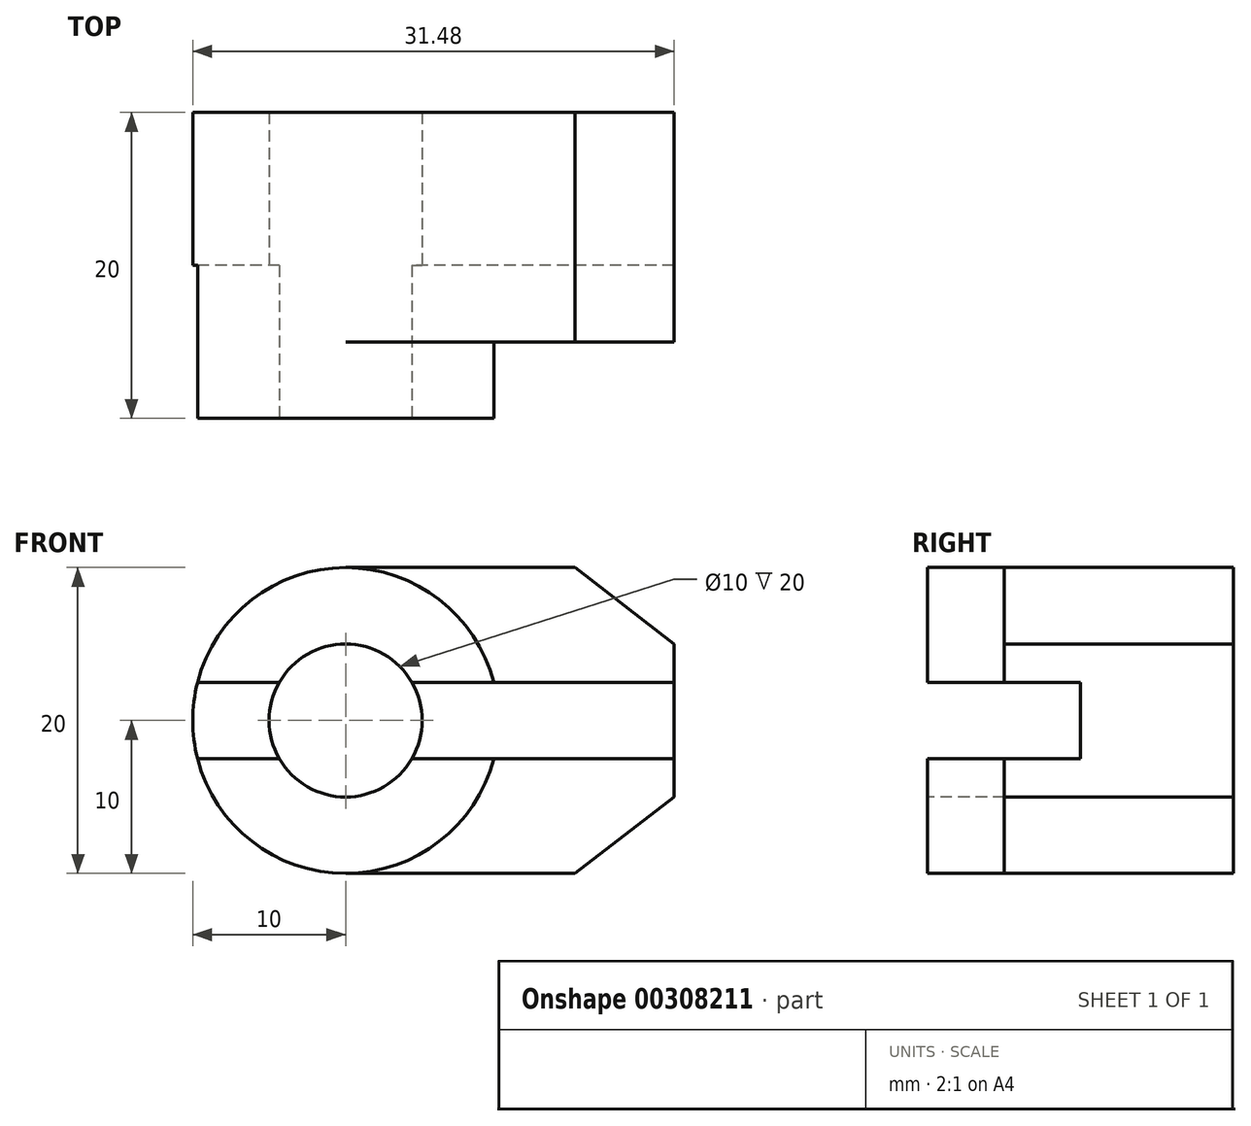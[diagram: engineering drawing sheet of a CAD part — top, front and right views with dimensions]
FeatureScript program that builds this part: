
annotation { "Feature Type Name" : "Feature", "Feature Type Description" : "" }
export const myFeature = defineFeature(function(context is Context, id is Id, definition is map)
    precondition{}
    {
        {
            var Q0;
            Q0=qCreatedBy(makeId("Front.planeOp"),FACE);
            var sketch = newSketch(context, id + "F0", { "sketchPlane" : qUnion([Q0])});
            skCircle(sketch, "E0", {"center": v(0, 10) * mm, "radius": 10 * mm});
            skSolve(sketch);
        }
        {
            var Q0;
            Q0=makeQuery(id+"F0.imprint","IMPRINT",FACE,{"disambiguationData":[TD([[makeQuery(id+"F0.imprint","IMPRINT",EDGE,{"derivedFrom":sQuery(id+"F0.wireOp",EDGE,"E0")}),1.0]])]});
            extrude(context, id + "F1", {"entities" : qUnion([Q0]), "depth" : 20 * mm});
        }
        {
            var Q0;
            Q0=makeQuery(id+"F1.opExtrude","CAP_FACE",FACE,{"disambiguationData":[OSD([sQuery(id+"F0.wireOp",EDGE,"E0")])],"isStart":false});
            var sketch = newSketch(context, id + "F2", { "sketchPlane" : qUnion([Q0])});
            skCircle(sketch, "E1", {"center": v(0, 10) * mm, "radius": 5 * mm});
            skSolve(sketch);
        }
        {
            var Q0;
            Q0=makeQuery(id+"F2.imprint","IMPRINT",FACE,{"disambiguationData":[TD([[makeQuery(id+"F2.imprint","IMPRINT",EDGE,{"derivedFrom":sQuery(id+"F2.wireOp",EDGE,"E1")}),1.0]])]});
            extrude(context, id + "F3", {"entities" : qUnion([Q0]), "operationType" : NewBodyOperationType.REMOVE, "endBound" : BoundingType.THROUGH_ALL, "oppositeDirection" : true, "depth" : 25 * mm});
        }
        {
            var Q0;
            Q0=makeQuery(id+"F1.opExtrude","CAP_FACE",FACE,{"disambiguationData":[OSD([sQuery(id+"F0.wireOp",EDGE,"E0")])],"isStart":false});
            cPlane(context, id + "F4", {"entities" : qUnion([Q0]), "cplaneType" : CPlaneType.OFFSET, "offset" : 5 * mm, "oppositeDirection" : true, "width" : 150 * mm, "height" : 150 * mm});
        }
        {
            var Q0;
            Q0 = qSketchRegion(id + "F2", true);
            extrude(context, id + "F5", {"entities" : qUnion([Q0]), "operationType" : NewBodyOperationType.REMOVE, "endBound" : BoundingType.THROUGH_ALL, "oppositeDirection" : true, "depth" : 25 * mm});
        }
        {
            var Q0;
            Q0=qCreatedBy(id+"F4.planeOp",FACE);
            var sketch = newSketch(context, id + "F6", { "sketchPlane" : qUnion([Q0])});
            skLineSegment(sketch, "E2", {"start": v(0, 20) * mm, "end": v(15, 20) * mm});
            skLineSegment(sketch, "E3", {"start": v(0, 0) * mm, "end": v(15, 0) * mm});
            skLineSegment(sketch, "E4", {"start": v(15, 0) * mm, "end": v(21.48, 5) * mm});
            skLineSegment(sketch, "E5", {"start": v(21.48, 5) * mm, "end": v(21.48, 15) * mm});
            skLineSegment(sketch, "E6", {"start": v(21.48, 15) * mm, "end": v(15, 20) * mm});
            skLineSegment(sketch, "E7", {"start": v(0, 20) * mm, "end": v(0, 0) * mm});
            skSolve(sketch);
        }
        {
            var Q0;
            Q0 = qSketchRegion(id + "F6", true);
            extrude(context, id + "F7", {"entities" : qUnion([Q0]), "operationType" : NewBodyOperationType.ADD, "oppositeDirection" : true, "depth" : 15 * mm});
        }
        {
            var Q0;
            {var subQ0=sQuery(id+"F6.wireOp",EDGE,"E7");Q0=makeQuery(id+"F7.boolean.opBoolean","SPLIT",FACE,{"disambiguationData":[TD([makeQuery(id+"F3.boolean.opBoolean","COPY",FACE,{"derivedFrom":makeQuery(id+"F3.opExtrude","SWEPT_FACE",FACE,{"disambiguationData":[OSD([sQuery(id+"F2.wireOp",EDGE,"E1")])]})})])],"derivedFrom":makeQuery(id+"F7.opExtrude","CAP_FACE",FACE,{"disambiguationData":[OSD([sQuery(id+"F6.wireOp",EDGE,"E2"),sQuery(id+"F6.wireOp",EDGE,"E3"),sQuery(id+"F6.wireOp",EDGE,"E4"),sQuery(id+"F6.wireOp",EDGE,"E5"),sQuery(id+"F6.wireOp",EDGE,"E6"),subQ0])],"isStart":true})});}
            extrude(context, id + "F8", {"entities" : qUnion([Q0]), "operationType" : NewBodyOperationType.REMOVE, "endBound" : BoundingType.THROUGH_ALL, "oppositeDirection" : true, "depth" : 25 * mm});
        }
        {
            var Q0;
            Q0=makeQuery(id+"F1.opExtrude","CAP_FACE",FACE,{"disambiguationData":[OSD([sQuery(id+"F0.wireOp",EDGE,"E0")])],"isStart":false});
            cPlane(context, id + "F9", {"entities" : qUnion([Q0]), "cplaneType" : CPlaneType.OFFSET, "offset" : 0 * mm, "width" : 150 * mm, "height" : 150 * mm});
        }
        {
            var Q0;
            Q0=qCreatedBy(id+"F9.planeOp",FACE);
            var sketch = newSketch(context, id + "F10", { "sketchPlane" : qUnion([Q0])});
            skLineSegment(sketch, "E8", {"start": v(23.98, 12.5) * mm, "end": v(-16.07, 12.5) * mm});
            skLineSegment(sketch, "E9", {"start": v(23.98, 7.5) * mm, "end": v(-16.07, 7.5) * mm});
            skLineSegment(sketch, "E10", {"start": v(-16.07, 7.5) * mm, "end": v(-16.07, 12.5) * mm});
            skLineSegment(sketch, "E11", {"start": v(23.98, 12.5) * mm, "end": v(23.98, 7.5) * mm});
            skLineSegment(sketch, "E12", {"start": v(23.98, 12.5) * mm, "end": v(21.48, 15) * mm, "construction": true});
            skLineSegment(sketch, "E13", {"start": v(23.98, 7.5) * mm, "end": v(21.48, 5) * mm, "construction": true});
            skSolve(sketch);
        }
        {
            var Q0;
            Q0 = qSketchRegion(id + "F10", true);
            extrude(context, id + "F11", {"entities" : qUnion([Q0]), "operationType" : NewBodyOperationType.REMOVE, "oppositeDirection" : true, "depth" : 10 * mm});
        }
    });
